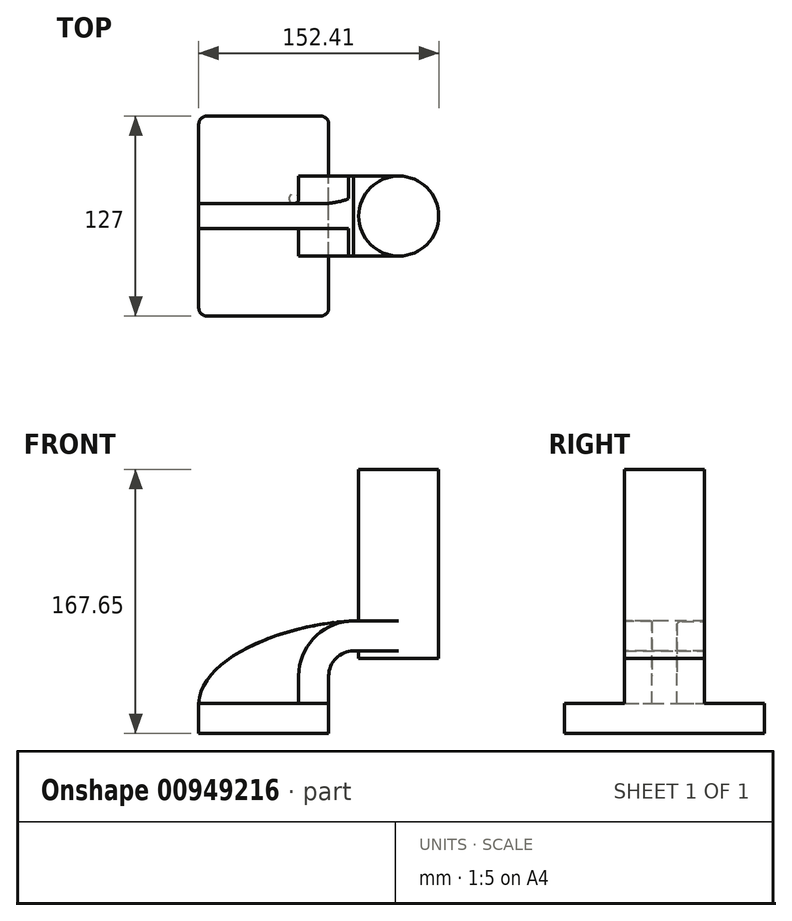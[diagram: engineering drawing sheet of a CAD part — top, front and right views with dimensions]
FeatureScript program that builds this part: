
annotation { "Feature Type Name" : "Feature", "Feature Type Description" : "" }
export const myFeature = defineFeature(function(context is Context, id is Id, definition is map)
    precondition{}
    {
        {
            var Q0;
            Q0=qCreatedBy(makeId("Front.planeOp"),FACE);
            var sketch = newSketch(context, id + "F0", { "sketchPlane" : qUnion([Q0])});
            skLineSegment(sketch, "E0.rect.bottom", {"start": v(-41.28, 9.52) * mm, "end": v(41.28, 9.52) * mm});
            skLineSegment(sketch, "E0.rect.top", {"start": v(-41.28, -9.52) * mm, "end": v(41.28, -9.52) * mm});
            skLineSegment(sketch, "E0.rect.left", {"start": v(-41.28, 9.52) * mm, "end": v(-41.28, -9.52) * mm});
            skLineSegment(sketch, "E0.rect.right", {"start": v(41.28, 9.52) * mm, "end": v(41.28, -9.52) * mm});
            skPoint(sketch, "E0.rect.middle", {"position": v(0, 0) * mm});
            skLineSegment(sketch, "E1", {"start": v(41.28, 9.52) * mm, "end": v(41.28, 27) * mm});
            skArc(sketch, "E2", {"start": v(41.28, 27) * mm, "mid": v(45.92, 38.23) * mm, "end": v(57.15, 42.88) * mm});
            skLineSegment(sketch, "E3", {"start": v(57.15, 42.88) * mm, "end": v(85.72, 42.88) * mm});
            skLineSegment(sketch, "E4.rect.bottom", {"start": v(60.32, 38.1) * mm, "end": v(111.12, 38.1) * mm});
            skLineSegment(sketch, "E4.rect.top", {"start": v(60.32, 66.68) * mm, "end": v(111.12, 66.68) * mm});
            skLineSegment(sketch, "E4.rect.left", {"start": v(60.32, 38.1) * mm, "end": v(60.32, 66.68) * mm});
            skLineSegment(sketch, "E4.rect.right", {"start": v(111.13, 38.1) * mm, "end": v(111.12, 66.68) * mm});
            skPoint(sketch, "E4.rect.middle", {"position": v(85.72, 52.39) * mm});
            skLineSegment(sketch, "E5.0", {"start": v(57.15, 61.93) * mm, "end": v(85.72, 61.93) * mm});
            skArc(sketch, "E5.1", {"start": v(22.23, 27) * mm, "mid": v(32.45, 51.7) * mm, "end": v(57.15, 61.93) * mm});
            skLineSegment(sketch, "E5.2", {"start": v(22.23, 9.52) * mm, "end": v(22.23, 27) * mm});
            skLineSegment(sketch, "E6", {"start": v(85.72, 38.1) * mm, "end": v(85.72, 66.68) * mm});
            skFitSpline(sketch, "E7", {"points": [v(-41.28, 9.53) * mm, v(57.15, 61.93) * mm], "startDerivative": vector(5.2, 92.34) * mm, "endDerivative": vector(120.92, 4.22) * mm});
            skSolve(sketch);
        }
        {
            var Q0;
            Q0=makeQuery(id+"F0.imprint","IMPRINT",FACE,{"disambiguationData":[TD([[makeQuery(id+"F0.imprint","IMPRINT",EDGE,{"derivedFrom":sQuery(id+"F0.wireOp",EDGE,"E0.rect.top")}),1.0]])]});
            extrude(context, id + "F1", {"entities" : qUnion([Q0]), "endBound" : BoundingType.SYMMETRIC, "depth" : 127 * mm});
        }
        {
            var Q0;
            {var subQ9=sQuery(id+"F0.wireOp",EDGE,"E1");Q0=makeQuery(id+"F0.imprint","IMPRINT",FACE,{"disambiguationData":[TD([[makeQuery(id+"F0.imprint","IMPRINT",EDGE,{"derivedFrom":subQ9}),1.0]])]});}
            var Q1;
            {var subQ0=sQuery(id+"F0.wireOp",EDGE,"E6");var subQ1=sQuery(id+"F0.wireOp",EDGE,"E3");var subQ2=makeQuery(id+"F0.imprint","INTERSECT",VERTEX,{"derivedFrom":[subQ1,subQ0]});Q1=makeQuery(id+"F0.imprint","IMPRINT",FACE,{"disambiguationData":[TD([[makeQuery(id+"F0.imprint","IMPRINT",EDGE,{"disambiguationData":[TD([[subQ2,1.0]])],"derivedFrom":subQ1}),1.0]])]});}
            extrude(context, id + "F2", {"entities" : qUnion([Q0, Q1]), "operationType" : NewBodyOperationType.ADD, "endBound" : BoundingType.SYMMETRIC, "offsetDistance" : 25.4 * mm, "depth" : 50.8 * mm});
        }
        {
            var Q0;
            {var subQ3=sQuery(id+"F0.wireOp",EDGE,"E5.2");Q0=makeQuery(id+"F0.imprint","IMPRINT",FACE,{"disambiguationData":[TD([[makeQuery(id+"F0.imprint","IMPRINT",EDGE,{"derivedFrom":subQ3}),1.0]])]});}
            extrude(context, id + "F3", {"entities" : qUnion([Q0]), "operationType" : NewBodyOperationType.ADD, "endBound" : BoundingType.SYMMETRIC, "depth" : 15.88 * mm});
        }
        {
            var Q0;
            {var subQ5=sQuery(id+"F0.wireOp",EDGE,"E4.rect.right");Q0=makeQuery(id+"F0.imprint","IMPRINT",FACE,{"disambiguationData":[TD([[makeQuery(id+"F0.imprint","IMPRINT",EDGE,{"derivedFrom":subQ5}),1.0]])]});}
            var Q1;
            Q1=sQuery(id+"F0.wireOp",EDGE,"E6");
            revolve(context, id + "F4", {"operationType" : NewBodyOperationType.ADD, "entities" : qUnion([Q0]), "axis" : qUnion([Q1]), "revolveType" : RevolveType.FULL});
        }
        {
            var Q0;
            Q0=makeQuery(id+"F1.opExtrude","CAP_EDGE",EDGE,{"disambiguationData":[OSD([sQuery(id+"F0.wireOp",EDGE,"E0.rect.right")])],"isStart":false});
            var Q1;
            Q1=makeQuery(id+"F1.opExtrude","CAP_EDGE",EDGE,{"disambiguationData":[OSD([sQuery(id+"F0.wireOp",EDGE,"E0.rect.left")])],"isStart":false});
            var Q2;
            Q2=makeQuery(id+"F1.opExtrude","CAP_EDGE",EDGE,{"disambiguationData":[OSD([sQuery(id+"F0.wireOp",EDGE,"E0.rect.right")])],"isStart":true});
            var Q3;
            Q3=makeQuery(id+"F1.opExtrude","CAP_EDGE",EDGE,{"disambiguationData":[OSD([sQuery(id+"F0.wireOp",EDGE,"E0.rect.left")])],"isStart":true});
            fillet(context, id + "F5", {"entities" : qUnion([Q0, Q1, Q2, Q3]), "radius" : 5.08 * mm, "tangentPropagation" : true, "allowEdgeOverflow" : false});
        }
        {
            var Q0;
            Q0=makeQuery(id+"F3.opExtrude","CAP_EDGE",EDGE,{"disambiguationData":[OSD([sQuery(id+"F0.wireOp",EDGE,"E5.1")])],"isStart":false});
            var Q1;
            Q1=makeQuery(id+"F3.opExtrude","CAP_EDGE",EDGE,{"disambiguationData":[OSD([sQuery(id+"F0.wireOp",EDGE,"E5.1")])],"isStart":true});
            fillet(context, id + "F6", {"entities" : qUnion([Q0, Q1]), "radius" : 3.07 * mm, "tangentPropagation" : true, "allowEdgeOverflow" : false});
        }
        {
            var Q0;
            Q0=makeQuery(id+"F4.opRevolve","SWEPT_FACE",FACE,{"disambiguationData":[OSD([sQuery(id+"F0.wireOp",EDGE,"E4.rect.top")])]});
            extrude(context, id + "F7", {"entities" : qUnion([Q0]), "operationType" : NewBodyOperationType.ADD, "depth" : 91.44 * mm, "offsetDistance" : 25.4 * mm});
        }
    });
